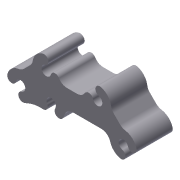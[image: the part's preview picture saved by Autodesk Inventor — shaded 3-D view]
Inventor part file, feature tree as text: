
AUTODESK INVENTOR PART (.ipt)
format: ipt  version: 2011 (Build 150239000, 239)  size: 145,920 bytes
history: native  units: in
note: dims shown in document units (in); Inventor stores cm internally (conversion verified against a paired STEP export)
features: extrude x1, sketch x1
ambient origin geometry x8: Origin, YZ Plane, XZ Plane, XY Plane, X Axis, Y Axis, Z Axis, Center Point
bodies: Solid1 (feature_tree)
feature tree (2):
  extrude  "Extrusion1"  [1 undecoded]
  sketch  "Sketch1"  dims[d0=0.995in d1=0.0in]
note: 1 required parameter value undecoded (feature->parameter linkage not recoverable at this tier; creation-order binding heuristic only, values carry confidence <= 0.55)
